# Revit family: Door_Pivot-Bifold_1Lite
name_source: partatom
category: Doors
units: mm (PartAtom-declared; Revit-internal decimal feet)

## family parameters
Always vertical = Yes
Classification Number = 23.30.10.17.17
Cut with Voids When Loaded = No
Host = Wall
Room Calculation Point = No
Shared = No

## types (2) — shared parameters
Analytic Construction = <None>
Assembly Code = C1020100
Clear Opening Height = 8' - 0"
Clear Opening Width = 3' - 0"
Description = Renin 2 Panel Steel Bifold Door - 4006 as Specified
Door Design = Panel_1Lite
Door Finish = Glass_Tempered_Frosted
Fire Rating = As Specified
Function = Interior
Hardware = Metal - Chrome - Hardware
Keynote = 08 00 00
Manufacturer = Renin Corp
Manufacturer Fax = 905-791-3813
Manufacturer Website = https://www.renin.com
Maximum Width = 0' - 0"
Minimum Width = 0' - 0"
Panel Thickness = 0' - 1 3/16"
Product Data = http://www.arcat.com
Sales Information = https://www.renin.com
Standards Conformance = Mirrored Doors conform to CGSB 12.5-M86 Type 3C and ANSI Z97.1-1984
Thickness = 0' - 0"
Type Comments = Confirm Opening Size Requirements
URL = https://www.renin.com
Wall Closure = By host
handlevis = No
handlevisb = No
mirroredswing = No
mirroredswingb = Yes
swing = Yes
swingb = No
zero-valued in all types: Expected Lifespan (Years), Maintenance Schedule (Months), Sound Transmission Class (STC), Warranty Duration (Years)

## per-type parameters (varying)
| type | Frame Finish |
| 5401 Espresso | Wood - Renin - Espresso |
| 5401 Off-White | Metal - Renin - Off-White |

note: column(s) folded — value = type name in every type: Model

## geometry (parser evidence)
native form markers: Blend x15, Sweep x7
no freeform markers — native parametric forms only
